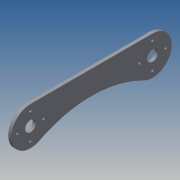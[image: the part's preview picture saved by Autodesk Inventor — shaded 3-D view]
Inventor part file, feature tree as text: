
AUTODESK INVENTOR PART (.ipt)
format: ipt  version: 2014 (Build 180170000, 170)  size: 106,496 bytes
history: native  units: mm
features: extrude x1, sketch x1
ambient origin geometry x8: Origin, YZ Plane, XZ Plane, XY Plane, X Axis, Y Axis, Z Axis, Center Point
bodies: Solid1 (feature_tree)
feature tree (2):
  extrude  "Extrusion1"  Depth=2.0mm TaperAngle=0.0deg
  sketch  "Sketch1"  dims[d0=79.5mm d1=25.0mm d2=25.0mm d3=7.0mm d4=1.5mm d5=1.5mm d6=1.5mm d7=8.5mm d8=8.5mm d9=8.5mm d10=1.5mm d11=8.5mm d12=7.0mm d13=1.5mm d14=1.5mm d15=1.5mm d16=1.5mm d17=8.5mm d18=8.5mm d19=8.5mm d20=8.5mm d21=2.0mm d22=0.0mm]
